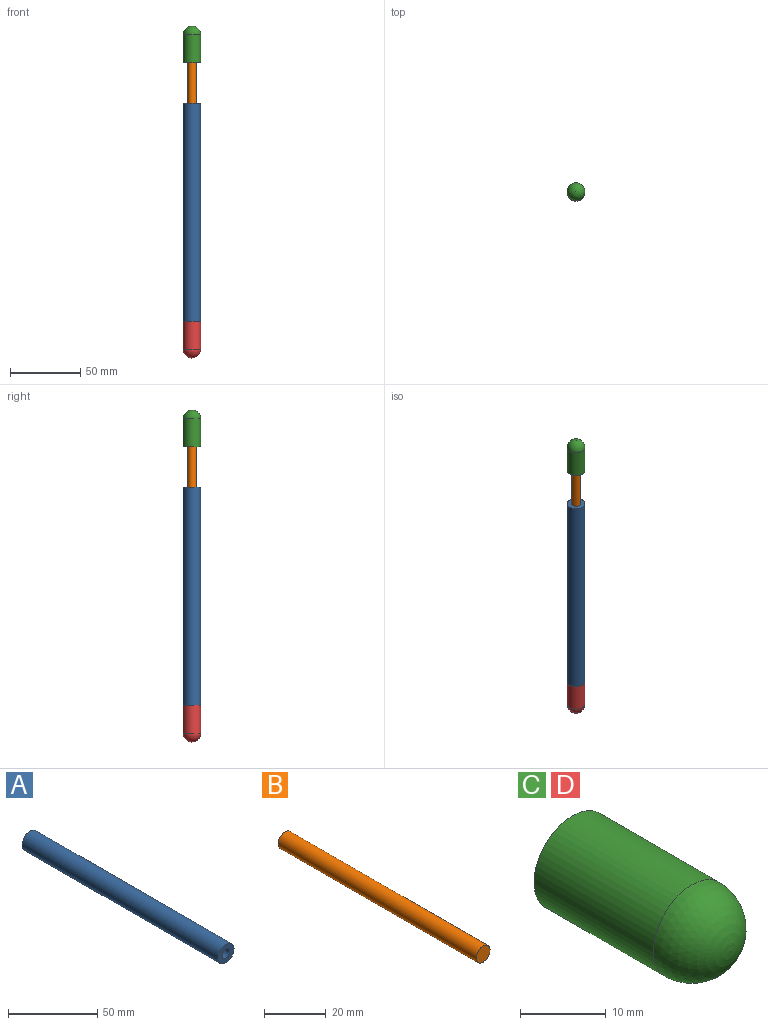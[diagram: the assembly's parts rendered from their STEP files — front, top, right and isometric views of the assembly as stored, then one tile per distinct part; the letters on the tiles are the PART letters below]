
ASSEMBLY  parts=4 mates=3
PART A: 4 faces, bbox 12.7x154.9x12.7 mm
  f0: cylinder r=3.17mm len=154.94mm, axis (0,1,0), area 3090.9mm2, adj f2,f3
  f1: cylinder r=6.35mm len=154.94mm, axis (0,1,0), area 6181.8mm2, adj f2,f3
  f2: plane 12.7x12.7mm, normal (0,-1,0), area 95mm2, adj f0,f1
  f3: plane 12.7x12.7mm, normal (0,1,0), area 95mm2, adj f0,f1
PART B: 3 faces, bbox 6.4x90.4x6.4 mm
  f0: cylinder r=3.17mm len=90.42mm, axis (0,1,0), area 1803.9mm2, adj f1,f2
  f1: plane 6.35x6.35mm, normal (0,-1,0), area 31.7mm2, adj f0
  f2: plane 6.35x6.35mm, normal (0,1,0), area 31.7mm2, adj f0
PART C: 3 faces, bbox 12.7x26.1x12.7 mm
  f0: plane 12.7x12.7mm, normal (0,1,0), area 126.7mm2, adj f1
  f1: cylinder r=6.35mm len=19.75mm, axis (0,1,0), area 787.9mm2, adj f0,f2
  f2: sphere r=6.35mm, area 253.4mm2, adj f1
PART D: same geometry as C
PLACE A rot(axis=(0,0.71,0.71),180deg) t=(0,0,0)mm
PLACE B rot(axis=(0.58,-0.58,-0.58),120deg) t=(0,0,28.94)mm
PLACE C rot(axis=(0,-0.71,0.71),180deg) t=(0,0,28.94)mm
PLACE D rot(axis=(1,0,0),90deg) t=(0,0,-154.94)mm
MATE fastened D.f1 <-> A.f1  axis (0,0,1) through (0,0,-154.94)mm
MATE cylindrical B.f0 <-> A.f1  axis (0,0,1) through (0,0,-16.27)mm
MATE fastened C.f1 <-> B.f0  axis (0,0,-1) through (0,0,28.94)mm
